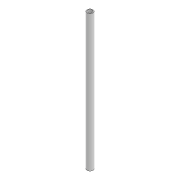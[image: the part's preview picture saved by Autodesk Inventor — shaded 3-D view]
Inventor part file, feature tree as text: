
AUTODESK INVENTOR PART (.ipt)
format: ipt  version: 2021 (Build 250183000, 183)  size: 96,768 bytes
history: native  units: mm
features: other x1, extrude x1, sketch x1
ambient origin geometry x8: Origin, YZ Plane, XZ Plane, XY Plane, X Axis, Y Axis, Z Axis, Center Point
bodies: Body1 (feature_tree)
feature tree (3):
  other  "Твердое тело1"
  extrude  "Выдавливание1"  Depth=1.0mm
  sketch  "Эскиз1"
